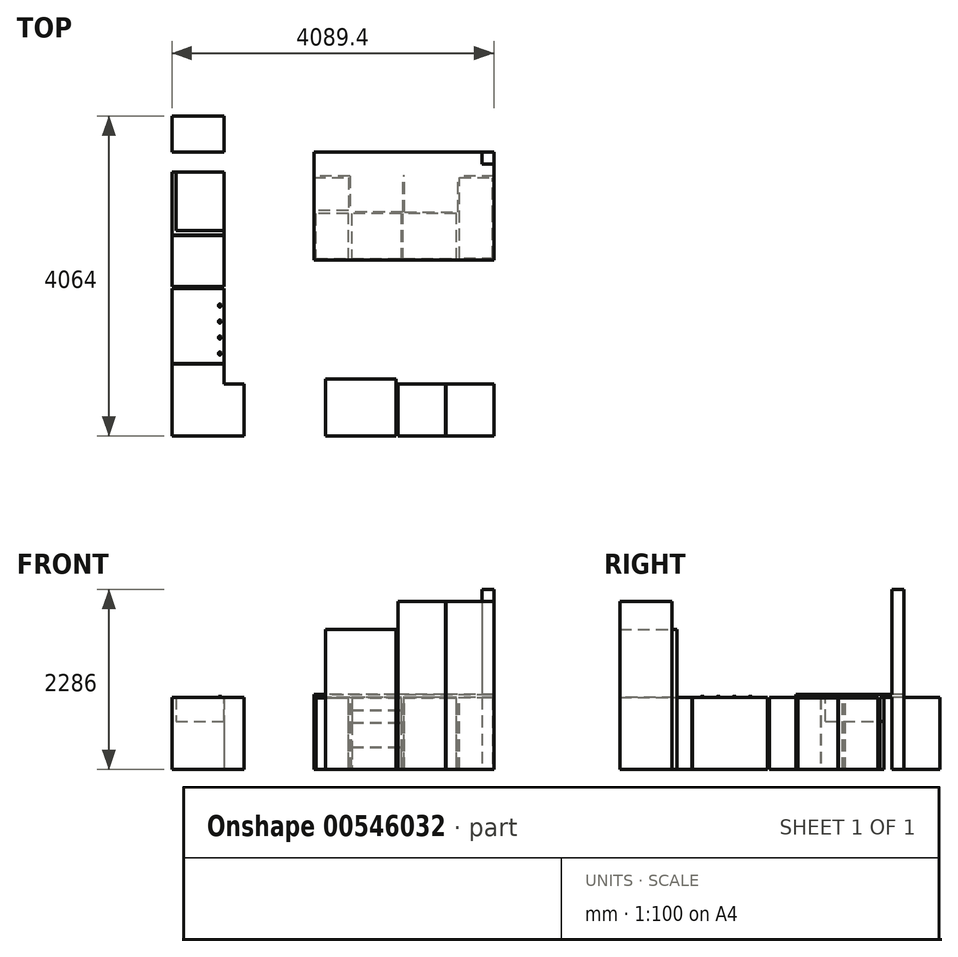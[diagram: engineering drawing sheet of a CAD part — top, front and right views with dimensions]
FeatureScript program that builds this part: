
annotation { "Feature Type Name" : "Feature", "Feature Type Description" : "" }
export const myFeature = defineFeature(function(context is Context, id is Id, definition is map)
    precondition{}
    {
        {
            var Q0;
            Q0=qCreatedBy(makeId("Top.planeOp"),FACE);
            var sketch = newSketch(context, id + "F0", { "sketchPlane" : qUnion([Q0])});
            skLineSegment(sketch, "E0.bottom", {"start": v(0, 0) * mm, "end": v(-152.4, 0) * mm});
            skLineSegment(sketch, "E0.top", {"start": v(0, -152.4) * mm, "end": v(-152.4, -152.4) * mm});
            skLineSegment(sketch, "E0.left", {"start": v(0, 0) * mm, "end": v(0, -152.4) * mm});
            skLineSegment(sketch, "E0.right", {"start": v(-152.4, 0) * mm, "end": v(-152.4, -152.4) * mm});
            skSolve(sketch);
        }
        {
            var Q0;
            Q0 = qSketchRegion(id + "F0", true);
            extrude(context, id + "F1", {"entities" : qUnion([Q0]), "depth" : 2286 * mm, "offsetDistance" : 25.4 * mm});
        }
        {
            var Q0;
            Q0=makeQuery(id+"F1.opExtrude","CAP_FACE",FACE,{"disambiguationData":[OSD([sQuery(id+"F0.wireOp",EDGE,"E0.bottom"),sQuery(id+"F0.wireOp",EDGE,"E0.top"),sQuery(id+"F0.wireOp",EDGE,"E0.left"),sQuery(id+"F0.wireOp",EDGE,"E0.right")])],"isStart":true});
            cPlane(context, id + "F2", {"entities" : qUnion([Q0]), "cplaneType" : CPlaneType.OFFSET, "offset" : 914.4 * mm, "oppositeDirection" : true, "width" : 152.4 * mm, "height" : 152.4 * mm});
        }
        {
            var Q0;
            Q0=qCreatedBy(id+"F2.planeOp",FACE);
            var sketch = newSketch(context, id + "F3", { "sketchPlane" : qUnion([Q0])});
            skLineSegment(sketch, "E1", {"start": v(0, 152.4) * mm, "end": v(0, 1371.6) * mm});
            skLineSegment(sketch, "E2", {"start": v(0, 1371.6) * mm, "end": v(-2286, 1371.6) * mm});
            skLineSegment(sketch, "E3", {"start": v(-2286, 1371.6) * mm, "end": v(-2286, 0) * mm});
            skLineSegment(sketch, "E4", {"start": v(-2286, 0) * mm, "end": v(-152.4, 0) * mm});
            skLineSegment(sketch, "E5", {"start": v(-152.4, 0) * mm, "end": v(-152.4, 152.4) * mm});
            skLineSegment(sketch, "E6", {"start": v(-152.4, 152.4) * mm, "end": v(0, 152.4) * mm});
            skSolve(sketch);
        }
        {
            var Q0;
            Q0 = qSketchRegion(id + "F3", true);
            extrude(context, id + "F4", {"entities" : qUnion([Q0]), "operationType" : NewBodyOperationType.ADD, "oppositeDirection" : true, "depth" : 38.1 * mm, "offsetDistance" : 25.4 * mm});
        }
        {
            var Q0;
            Q0=makeQuery(id+"F4.opExtrude","CAP_FACE",FACE,{"disambiguationData":[OSD([sQuery(id+"F3.wireOp",EDGE,"E1"),sQuery(id+"F3.wireOp",EDGE,"E2"),sQuery(id+"F3.wireOp",EDGE,"E3"),sQuery(id+"F3.wireOp",EDGE,"E4"),sQuery(id+"F3.wireOp",EDGE,"E5"),sQuery(id+"F3.wireOp",EDGE,"E6")])],"isStart":false});
            var sketch = newSketch(context, id + "F5", { "sketchPlane" : qUnion([Q0])});
            skLineSegment(sketch, "E7", {"start": v(-2286, -304.8) * mm, "end": v(0, -304.8) * mm});
            skSolve(sketch);
        }
        {
            var Q0;
            Q0=makeQuery(id+"F4.opExtrude","CAP_FACE",FACE,{"disambiguationData":[OSD([sQuery(id+"F3.wireOp",EDGE,"E1"),sQuery(id+"F3.wireOp",EDGE,"E2"),sQuery(id+"F3.wireOp",EDGE,"E3"),sQuery(id+"F3.wireOp",EDGE,"E4"),sQuery(id+"F3.wireOp",EDGE,"E5"),sQuery(id+"F3.wireOp",EDGE,"E6")])],"isStart":true});
            var sketch = newSketch(context, id + "F6", { "sketchPlane" : qUnion([Q0])});
            skLineSegment(sketch, "E8.bottom", {"start": v(0, 1371.6) * mm, "end": v(-457.2, 1371.6) * mm});
            skLineSegment(sketch, "E8.top", {"start": v(0, 304.8) * mm, "end": v(-457.2, 304.8) * mm});
            skLineSegment(sketch, "E8.left", {"start": v(0, 1371.6) * mm, "end": v(0, 1352.55) * mm});
            skLineSegment(sketch, "E8.right", {"start": v(-457.2, 1371.6) * mm, "end": v(-457.2, 304.8) * mm});
            skLineSegment(sketch, "E9", {"start": v(0, 1352.55) * mm, "end": v(-438.15, 1352.55) * mm});
            skLineSegment(sketch, "E10", {"start": v(-438.15, 1352.55) * mm, "end": v(-438.15, 323.85) * mm});
            skLineSegment(sketch, "E11", {"start": v(-438.15, 323.85) * mm, "end": v(0, 323.85) * mm});
            skLineSegment(sketch, "E12.trimOffspring", {"start": v(0, 323.85) * mm, "end": v(0, 304.8) * mm});
            skSolve(sketch);
        }
        {
            var Q0;
            Q0 = qSketchRegion(id + "F6", true);
            var Q1;
            Q1=makeQuery(id+"F1.opExtrude","CAP_FACE",FACE,{"disambiguationData":[OSD([sQuery(id+"F0.wireOp",EDGE,"E0.bottom"),sQuery(id+"F0.wireOp",EDGE,"E0.top"),sQuery(id+"F0.wireOp",EDGE,"E0.left"),sQuery(id+"F0.wireOp",EDGE,"E0.right")])],"isStart":true});
            extrude(context, id + "F7", {"entities" : qUnion([Q0]), "operationType" : NewBodyOperationType.ADD, "endBound" : BoundingType.UP_TO_SURFACE, "depth" : 25.4 * mm, "endBoundEntityFace" : qUnion([Q1]), "offsetDistance" : 25.4 * mm});
        }
        {
            var Q0;
            {var subQ0=sQuery(id+"F3.wireOp",EDGE,"E4");var subQ1=sQuery(id+"F3.wireOp",EDGE,"E3");var subQ2=sQuery(id+"F3.wireOp",EDGE,"E2");var subQ3=sQuery(id+"F3.wireOp",EDGE,"E1");Q0=makeQuery(id+"F7.boolean.opBoolean","SPLIT",FACE,{"disambiguationData":[TD([makeQuery(id+"F1.opExtrude","SWEPT_FACE",FACE,{"disambiguationData":[OSD([sQuery(id+"F0.wireOp",EDGE,"E0.bottom")])]})])],"derivedFrom":makeQuery(id+"F4.opExtrude","CAP_FACE",FACE,{"disambiguationData":[OSD([subQ3,subQ2,subQ1,subQ0,sQuery(id+"F3.wireOp",EDGE,"E5"),sQuery(id+"F3.wireOp",EDGE,"E6")])],"isStart":true})});}
            var sketch = newSketch(context, id + "F8", { "sketchPlane" : qUnion([Q0])});
            skLineSegment(sketch, "E13", {"start": v(-2286, 1371.6) * mm, "end": v(-2286, 762) * mm});
            skLineSegment(sketch, "E14", {"start": v(-2286, 762) * mm, "end": v(-1828.8, 762) * mm});
            skLineSegment(sketch, "E15", {"start": v(-1828.8, 762) * mm, "end": v(-1828.8, 1371.6) * mm});
            skLineSegment(sketch, "E16", {"start": v(-1828.8, 1371.6) * mm, "end": v(-1847.85, 1371.6) * mm});
            skLineSegment(sketch, "E17", {"start": v(-1847.85, 1371.6) * mm, "end": v(-1847.85, 781.05) * mm});
            skLineSegment(sketch, "E18", {"start": v(-1847.85, 781.05) * mm, "end": v(-2266.95, 781.05) * mm});
            skLineSegment(sketch, "E19", {"start": v(-2266.95, 781.05) * mm, "end": v(-2266.95, 1371.6) * mm});
            skLineSegment(sketch, "E20", {"start": v(-2266.95, 1371.6) * mm, "end": v(-2286, 1371.6) * mm});
            skSolve(sketch);
        }
        {
            var Q0;
            Q0 = qSketchRegion(id + "F8", true);
            var Q1;
            Q1=makeQuery(id+"F1.opExtrude","CAP_FACE",FACE,{"disambiguationData":[OSD([sQuery(id+"F0.wireOp",EDGE,"E0.bottom"),sQuery(id+"F0.wireOp",EDGE,"E0.top"),sQuery(id+"F0.wireOp",EDGE,"E0.left"),sQuery(id+"F0.wireOp",EDGE,"E0.right")])],"isStart":true});
            extrude(context, id + "F9", {"entities" : qUnion([Q0]), "operationType" : NewBodyOperationType.ADD, "endBound" : BoundingType.UP_TO_SURFACE, "depth" : 25.4 * mm, "endBoundEntityFace" : qUnion([Q1]), "offsetDistance" : 25.4 * mm});
        }
        {
            var Q0;
            {var subQ2=sQuery(id+"F3.wireOp",EDGE,"E4");var subQ4=sQuery(id+"F3.wireOp",EDGE,"E3");var subQ6=sQuery(id+"F3.wireOp",EDGE,"E2");var subQ8=makeQuery(id+"F1.opExtrude","SWEPT_FACE",FACE,{"disambiguationData":[OSD([sQuery(id+"F0.wireOp",EDGE,"E0.bottom")])]});var subQ9=sQuery(id+"F3.wireOp",EDGE,"E1");Q0=makeQuery(id+"F9.boolean.opBoolean","SPLIT",FACE,{"disambiguationData":[TD([subQ8])],"derivedFrom":makeQuery(id+"F7.boolean.opBoolean","SPLIT",FACE,{"disambiguationData":[TD([subQ8])],"derivedFrom":makeQuery(id+"F4.opExtrude","CAP_FACE",FACE,{"disambiguationData":[OSD([subQ9,subQ6,subQ4,subQ2,sQuery(id+"F3.wireOp",EDGE,"E5"),sQuery(id+"F3.wireOp",EDGE,"E6")])],"isStart":true})})});}
            var sketch = newSketch(context, id + "F10", { "sketchPlane" : qUnion([Q0])});
            skLineSegment(sketch, "E21", {"start": v(-2286, 762) * mm, "end": v(-1828.8, 762) * mm});
            skLineSegment(sketch, "E22", {"start": v(-1828.8, 762) * mm, "end": v(-1828.8, 304.8) * mm});
            skLineSegment(sketch, "E23", {"start": v(-1828.8, 304.8) * mm, "end": v(-2286, 304.8) * mm});
            skLineSegment(sketch, "E24", {"start": v(-2286, 304.8) * mm, "end": v(-2286, 323.85) * mm});
            skLineSegment(sketch, "E25", {"start": v(-2286, 323.85) * mm, "end": v(-1847.85, 323.85) * mm});
            skLineSegment(sketch, "E26", {"start": v(-1847.85, 323.85) * mm, "end": v(-1847.85, 742.95) * mm});
            skLineSegment(sketch, "E27", {"start": v(-1847.85, 742.95) * mm, "end": v(-2286, 742.95) * mm});
            skLineSegment(sketch, "E28", {"start": v(-2286, 742.95) * mm, "end": v(-2286, 762) * mm});
            skSolve(sketch);
        }
        {
            var Q0;
            Q0 = qSketchRegion(id + "F10", true);
            var Q1;
            Q1=makeQuery(id+"F9.opExtrude","CAP_FACE",FACE,{"disambiguationData":[OSD([sQuery(id+"F8.wireOp",EDGE,"E13"),sQuery(id+"F8.wireOp",EDGE,"E14"),sQuery(id+"F8.wireOp",EDGE,"E15"),sQuery(id+"F8.wireOp",EDGE,"E16"),sQuery(id+"F8.wireOp",EDGE,"E17"),sQuery(id+"F8.wireOp",EDGE,"E18"),sQuery(id+"F8.wireOp",EDGE,"E19"),sQuery(id+"F8.wireOp",EDGE,"E20")])],"isStart":false});
            extrude(context, id + "F11", {"entities" : qUnion([Q0]), "operationType" : NewBodyOperationType.ADD, "endBound" : BoundingType.UP_TO_SURFACE, "depth" : 25.4 * mm, "endBoundEntityFace" : qUnion([Q1]), "offsetDistance" : 25.4 * mm});
        }
        {
            var Q0;
            {var subQ2=sQuery(id+"F3.wireOp",EDGE,"E4");var subQ4=sQuery(id+"F3.wireOp",EDGE,"E3");var subQ6=sQuery(id+"F3.wireOp",EDGE,"E2");var subQ9=makeQuery(id+"F1.opExtrude","SWEPT_FACE",FACE,{"disambiguationData":[OSD([sQuery(id+"F0.wireOp",EDGE,"E0.bottom")])]});var subQ10=sQuery(id+"F3.wireOp",EDGE,"E1");Q0=makeQuery(id+"F11.boolean.opBoolean","SPLIT",FACE,{"disambiguationData":[TD([subQ9])],"derivedFrom":makeQuery(id+"F9.boolean.opBoolean","SPLIT",FACE,{"disambiguationData":[TD([subQ9])],"derivedFrom":makeQuery(id+"F7.boolean.opBoolean","SPLIT",FACE,{"disambiguationData":[TD([subQ9])],"derivedFrom":makeQuery(id+"F4.opExtrude","CAP_FACE",FACE,{"disambiguationData":[OSD([subQ10,subQ6,subQ4,subQ2,sQuery(id+"F3.wireOp",EDGE,"E5"),sQuery(id+"F3.wireOp",EDGE,"E6")])],"isStart":true})})})});}
            var sketch = newSketch(context, id + "F12", { "sketchPlane" : qUnion([Q0])});
            skLineSegment(sketch, "E29", {"start": v(-1828.8, 1371.6) * mm, "end": v(-1828.8, 762) * mm});
            skLineSegment(sketch, "E30", {"start": v(-1828.8, 762) * mm, "end": v(-457.2, 762) * mm});
            skLineSegment(sketch, "E31", {"start": v(-457.2, 762) * mm, "end": v(-457.2, 1371.6) * mm});
            skLineSegment(sketch, "E32", {"start": v(-457.2, 1371.6) * mm, "end": v(-476.25, 1371.6) * mm});
            skLineSegment(sketch, "E33", {"start": v(-476.25, 1371.6) * mm, "end": v(-476.25, 781.05) * mm});
            skLineSegment(sketch, "E34", {"start": v(-476.25, 781.05) * mm, "end": v(-1809.75, 781.05) * mm});
            skLineSegment(sketch, "E35", {"start": v(-1809.75, 781.05) * mm, "end": v(-1809.75, 1371.6) * mm});
            skLineSegment(sketch, "E36", {"start": v(-1809.75, 1371.6) * mm, "end": v(-1828.8, 1371.6) * mm});
            skSolve(sketch);
        }
        {
            var Q0;
            Q0 = qSketchRegion(id + "F12", true);
            var Q1;
            Q1=makeQuery(id+"F1.opExtrude","CAP_FACE",FACE,{"disambiguationData":[OSD([sQuery(id+"F0.wireOp",EDGE,"E0.bottom"),sQuery(id+"F0.wireOp",EDGE,"E0.top"),sQuery(id+"F0.wireOp",EDGE,"E0.left"),sQuery(id+"F0.wireOp",EDGE,"E0.right")])],"isStart":true});
            extrude(context, id + "F13", {"entities" : qUnion([Q0]), "operationType" : NewBodyOperationType.ADD, "endBound" : BoundingType.UP_TO_SURFACE, "depth" : 25.4 * mm, "endBoundEntityFace" : qUnion([Q1]), "offsetDistance" : 25.4 * mm});
        }
        {
            var Q0;
            {var subQ3=sQuery(id+"F3.wireOp",EDGE,"E2");var subQ4=makeQuery(id+"F4.opExtrude","SWEPT_FACE",FACE,{"disambiguationData":[OSD([subQ3])]});var subQ6=sQuery(id+"F3.wireOp",EDGE,"E4");var subQ8=sQuery(id+"F3.wireOp",EDGE,"E3");var subQ10=makeQuery(id+"F1.opExtrude","SWEPT_FACE",FACE,{"disambiguationData":[OSD([sQuery(id+"F0.wireOp",EDGE,"E0.bottom")])]});var subQ11=sQuery(id+"F3.wireOp",EDGE,"E1");Q0=makeQuery(id+"F13.boolean.opBoolean","SPLIT",FACE,{"disambiguationData":[TD([subQ4])],"derivedFrom":makeQuery(id+"F11.boolean.opBoolean","SPLIT",FACE,{"disambiguationData":[TD([subQ10])],"derivedFrom":makeQuery(id+"F9.boolean.opBoolean","SPLIT",FACE,{"disambiguationData":[TD([subQ10])],"derivedFrom":makeQuery(id+"F7.boolean.opBoolean","SPLIT",FACE,{"disambiguationData":[TD([subQ10])],"derivedFrom":makeQuery(id+"F4.opExtrude","CAP_FACE",FACE,{"disambiguationData":[OSD([subQ11,subQ3,subQ8,subQ6,sQuery(id+"F3.wireOp",EDGE,"E5"),sQuery(id+"F3.wireOp",EDGE,"E6")])],"isStart":true})})})})});}
            var sketch = newSketch(context, id + "F14", { "sketchPlane" : qUnion([Q0])});
            skLineSegment(sketch, "E37.bottom", {"start": v(-1174.75, 1371.6) * mm, "end": v(-1155.7, 1371.6) * mm});
            skLineSegment(sketch, "E37.top", {"start": v(-1174.75, 781.05) * mm, "end": v(-1155.7, 781.05) * mm});
            skLineSegment(sketch, "E37.left", {"start": v(-1174.75, 1371.6) * mm, "end": v(-1174.75, 781.05) * mm});
            skLineSegment(sketch, "E37.right", {"start": v(-1155.7, 1371.6) * mm, "end": v(-1155.7, 781.05) * mm});
            skSolve(sketch);
        }
        {
            var Q0;
            Q0 = qSketchRegion(id + "F14", true);
            var Q1;
            Q1=makeQuery(id+"F1.opExtrude","CAP_FACE",FACE,{"disambiguationData":[OSD([sQuery(id+"F0.wireOp",EDGE,"E0.bottom"),sQuery(id+"F0.wireOp",EDGE,"E0.top"),sQuery(id+"F0.wireOp",EDGE,"E0.left"),sQuery(id+"F0.wireOp",EDGE,"E0.right")])],"isStart":true});
            extrude(context, id + "F15", {"entities" : qUnion([Q0]), "operationType" : NewBodyOperationType.ADD, "endBound" : BoundingType.UP_TO_SURFACE, "depth" : 25.4 * mm, "endBoundEntityFace" : qUnion([Q1]), "offsetDistance" : 25.4 * mm});
        }
        {
            var Q0;
            {var subQ3=sQuery(id+"F3.wireOp",EDGE,"E4");var subQ5=sQuery(id+"F3.wireOp",EDGE,"E3");var subQ8=makeQuery(id+"F1.opExtrude","SWEPT_FACE",FACE,{"disambiguationData":[OSD([sQuery(id+"F0.wireOp",EDGE,"E0.bottom")])]});var subQ9=sQuery(id+"F3.wireOp",EDGE,"E1");var subQ21=sQuery(id+"F3.wireOp",EDGE,"E2");Q0=makeQuery(id+"F13.boolean.opBoolean","SPLIT",FACE,{"disambiguationData":[TD([subQ8])],"derivedFrom":makeQuery(id+"F11.boolean.opBoolean","SPLIT",FACE,{"disambiguationData":[TD([subQ8])],"derivedFrom":makeQuery(id+"F9.boolean.opBoolean","SPLIT",FACE,{"disambiguationData":[TD([subQ8])],"derivedFrom":makeQuery(id+"F7.boolean.opBoolean","SPLIT",FACE,{"disambiguationData":[TD([subQ8])],"derivedFrom":makeQuery(id+"F4.opExtrude","CAP_FACE",FACE,{"disambiguationData":[OSD([subQ9,subQ21,subQ5,subQ3,sQuery(id+"F3.wireOp",EDGE,"E5"),sQuery(id+"F3.wireOp",EDGE,"E6")])],"isStart":true})})})})});}
            var sketch = newSketch(context, id + "F16", { "sketchPlane" : qUnion([Q0])});
            skLineSegment(sketch, "E38.bottom", {"start": v(-1133.47, 762) * mm, "end": v(-1152.52, 762) * mm});
            skLineSegment(sketch, "E38.top", {"start": v(-1133.47, 304.8) * mm, "end": v(-1152.52, 304.8) * mm});
            skLineSegment(sketch, "E38.left", {"start": v(-1133.47, 762) * mm, "end": v(-1133.47, 304.8) * mm});
            skLineSegment(sketch, "E38.right", {"start": v(-1152.52, 762) * mm, "end": v(-1152.52, 304.8) * mm});
            skSolve(sketch);
        }
        {
            var Q0;
            Q0 = qSketchRegion(id + "F16", true);
            var Q1;
            Q1=makeQuery(id+"F15.boolean.opBoolean","MERGE",FACE,{"derivedFrom":[makeQuery(id+"F13.boolean.opBoolean","MERGE",FACE,{"derivedFrom":[makeQuery(id+"F7.opExtrude","CAP_FACE",FACE,{"disambiguationData":[OSD([sQuery(id+"F6.wireOp",EDGE,"E8.bottom"),sQuery(id+"F6.wireOp",EDGE,"E8.top"),sQuery(id+"F6.wireOp",EDGE,"E8.left"),sQuery(id+"F6.wireOp",EDGE,"E8.right"),sQuery(id+"F6.wireOp",EDGE,"E9"),sQuery(id+"F6.wireOp",EDGE,"E10"),sQuery(id+"F6.wireOp",EDGE,"E11"),sQuery(id+"F6.wireOp",EDGE,"E12.trimOffspring")])],"isStart":false}),makeQuery(id+"F11.boolean.opBoolean","MERGE",FACE,{"derivedFrom":[makeQuery(id+"F9.opExtrude","CAP_FACE",FACE,{"disambiguationData":[OSD([sQuery(id+"F8.wireOp",EDGE,"E13"),sQuery(id+"F8.wireOp",EDGE,"E14"),sQuery(id+"F8.wireOp",EDGE,"E15"),sQuery(id+"F8.wireOp",EDGE,"E16"),sQuery(id+"F8.wireOp",EDGE,"E17"),sQuery(id+"F8.wireOp",EDGE,"E18"),sQuery(id+"F8.wireOp",EDGE,"E19"),sQuery(id+"F8.wireOp",EDGE,"E20")])],"isStart":false}),makeQuery(id+"F11.opExtrude","CAP_FACE",FACE,{"disambiguationData":[OSD([sQuery(id+"F10.wireOp",EDGE,"E21"),sQuery(id+"F10.wireOp",EDGE,"E22"),sQuery(id+"F10.wireOp",EDGE,"E23"),sQuery(id+"F10.wireOp",EDGE,"E24"),sQuery(id+"F10.wireOp",EDGE,"E25"),sQuery(id+"F10.wireOp",EDGE,"E26"),sQuery(id+"F10.wireOp",EDGE,"E27"),sQuery(id+"F10.wireOp",EDGE,"E28")])],"isStart":false})]}),makeQuery(id+"F13.opExtrude","CAP_FACE",FACE,{"disambiguationData":[OSD([sQuery(id+"F12.wireOp",EDGE,"E29"),sQuery(id+"F12.wireOp",EDGE,"E30"),sQuery(id+"F12.wireOp",EDGE,"E31"),sQuery(id+"F12.wireOp",EDGE,"E32"),sQuery(id+"F12.wireOp",EDGE,"E33"),sQuery(id+"F12.wireOp",EDGE,"E34"),sQuery(id+"F12.wireOp",EDGE,"E35"),sQuery(id+"F12.wireOp",EDGE,"E36")])],"isStart":false})]}),makeQuery(id+"F15.opExtrude","CAP_FACE",FACE,{"disambiguationData":[OSD([sQuery(id+"F14.wireOp",EDGE,"E37.bottom"),sQuery(id+"F14.wireOp",EDGE,"E37.top"),sQuery(id+"F14.wireOp",EDGE,"E37.left"),sQuery(id+"F14.wireOp",EDGE,"E37.right")])],"isStart":false})]});
            extrude(context, id + "F17", {"entities" : qUnion([Q0]), "operationType" : NewBodyOperationType.ADD, "endBound" : BoundingType.UP_TO_SURFACE, "depth" : 25.4 * mm, "endBoundEntityFace" : qUnion([Q1]), "offsetDistance" : 25.4 * mm});
        }
        {
            var Q0;
            Q0=makeQuery(id+"F7.boolean.opBoolean","MERGE",FACE,{"derivedFrom":[makeQuery(id+"F4.boolean.opBoolean","MERGE",FACE,{"derivedFrom":[makeQuery(id+"F1.opExtrude","SWEPT_FACE",FACE,{"disambiguationData":[OSD([sQuery(id+"F0.wireOp",EDGE,"E0.left")])]}),makeQuery(id+"F4.opExtrude","SWEPT_FACE",FACE,{"disambiguationData":[OSD([sQuery(id+"F3.wireOp",EDGE,"E1")])]})]}),makeQuery(id+"F7.opExtrude","SWEPT_FACE",FACE,{"disambiguationData":[OSD([sQuery(id+"F6.wireOp",EDGE,"E8.left")])]}),makeQuery(id+"F7.opExtrude","SWEPT_FACE",FACE,{"disambiguationData":[OSD([sQuery(id+"F6.wireOp",EDGE,"E12.trimOffspring")])]})]});
            var sketch = newSketch(context, id + "F18", { "sketchPlane" : qUnion([Q0])});
            skPoint(sketch, "E39.oppositeSnap0", {"position": v(-838.2, 914.4) * mm});
            skLineSegment(sketch, "E39.bottom", {"start": v(-1346.2, 908.05) * mm, "end": v(-838.2, 908.05) * mm});
            skLineSegment(sketch, "E39.top", {"start": v(-1346.2, 0) * mm, "end": v(-838.2, 0) * mm});
            skLineSegment(sketch, "E39.left", {"start": v(-1346.2, 908.05) * mm, "end": v(-1346.2, 0) * mm});
            skLineSegment(sketch, "E39.right", {"start": v(-838.2, 908.05) * mm, "end": v(-838.2, 0) * mm});
            skSolve(sketch);
        }
        {
            var Q0;
            Q0 = qSketchRegion(id + "F18", true);
            extrude(context, id + "F19", {"entities" : qUnion([Q0]), "oppositeDirection" : true, "depth" : 19.05 * mm, "offsetDistance" : 25.4 * mm});
        }
        {
            var Q0;
            Q0=makeQuery(id+"F7.boolean.opBoolean","MERGE",FACE,{"derivedFrom":[makeQuery(id+"F4.boolean.opBoolean","MERGE",FACE,{"derivedFrom":[makeQuery(id+"F1.opExtrude","SWEPT_FACE",FACE,{"disambiguationData":[OSD([sQuery(id+"F0.wireOp",EDGE,"E0.left")])]}),makeQuery(id+"F4.opExtrude","SWEPT_FACE",FACE,{"disambiguationData":[OSD([sQuery(id+"F3.wireOp",EDGE,"E1")])]})]}),makeQuery(id+"F7.opExtrude","SWEPT_FACE",FACE,{"disambiguationData":[OSD([sQuery(id+"F6.wireOp",EDGE,"E8.left")])]}),makeQuery(id+"F7.opExtrude","SWEPT_FACE",FACE,{"disambiguationData":[OSD([sQuery(id+"F6.wireOp",EDGE,"E12.trimOffspring")])]})]});
            var sketch = newSketch(context, id + "F20", { "sketchPlane" : qUnion([Q0])});
            skPoint(sketch, "E40.firstSnap0", {"position": v(-831.85, 914.4) * mm});
            skLineSegment(sketch, "E40.bottom", {"start": v(-831.85, 908.05) * mm, "end": v(-330.2, 908.05) * mm});
            skLineSegment(sketch, "E40.top", {"start": v(-831.85, 0) * mm, "end": v(-330.2, 0) * mm});
            skLineSegment(sketch, "E40.left", {"start": v(-831.85, 908.05) * mm, "end": v(-831.85, 0) * mm});
            skLineSegment(sketch, "E40.right", {"start": v(-330.2, 908.05) * mm, "end": v(-330.2, 0) * mm});
            skSolve(sketch);
        }
        {
            var Q0;
            Q0 = qSketchRegion(id + "F20", true);
            extrude(context, id + "F21", {"entities" : qUnion([Q0]), "operationType" : NewBodyOperationType.ADD, "oppositeDirection" : true, "depth" : 19.05 * mm, "offsetDistance" : 25.4 * mm});
        }
        {
            var Q0;
            Q0=makeQuery(id+"F15.boolean.opBoolean","MERGE",FACE,{"derivedFrom":[makeQuery(id+"F13.boolean.opBoolean","MERGE",FACE,{"derivedFrom":[makeQuery(id+"F9.boolean.opBoolean","MERGE",FACE,{"derivedFrom":[makeQuery(id+"F7.boolean.opBoolean","MERGE",FACE,{"derivedFrom":[makeQuery(id+"F4.opExtrude","SWEPT_FACE",FACE,{"disambiguationData":[OSD([sQuery(id+"F3.wireOp",EDGE,"E2")])]}),makeQuery(id+"F7.opExtrude","SWEPT_FACE",FACE,{"disambiguationData":[OSD([sQuery(id+"F6.wireOp",EDGE,"E8.bottom")])]})]}),makeQuery(id+"F9.opExtrude","SWEPT_FACE",FACE,{"disambiguationData":[OSD([sQuery(id+"F8.wireOp",EDGE,"E16")])]}),makeQuery(id+"F9.opExtrude","SWEPT_FACE",FACE,{"disambiguationData":[OSD([sQuery(id+"F8.wireOp",EDGE,"E20")])]})]}),makeQuery(id+"F13.opExtrude","SWEPT_FACE",FACE,{"disambiguationData":[OSD([sQuery(id+"F12.wireOp",EDGE,"E32")])]}),makeQuery(id+"F13.opExtrude","SWEPT_FACE",FACE,{"disambiguationData":[OSD([sQuery(id+"F12.wireOp",EDGE,"E36")])]})]}),makeQuery(id+"F15.opExtrude","SWEPT_FACE",FACE,{"disambiguationData":[OSD([sQuery(id+"F14.wireOp",EDGE,"E37.bottom")])]})]});
            var sketch = newSketch(context, id + "F22", { "sketchPlane" : qUnion([Q0])});
            skLineSegment(sketch, "E41.bottom", {"start": v(-1803.4, 908.05) * mm, "end": v(-1181.1, 908.05) * mm});
            skLineSegment(sketch, "E41.top", {"start": v(-1803.4, 755.65) * mm, "end": v(-1181.1, 755.65) * mm});
            skLineSegment(sketch, "E41.left", {"start": v(-1803.4, 908.05) * mm, "end": v(-1803.4, 755.65) * mm});
            skLineSegment(sketch, "E41.right", {"start": v(-1181.1, 908.05) * mm, "end": v(-1181.1, 755.65) * mm});
            skLineSegment(sketch, "E42.bottom", {"start": v(-1803.4, 749.3) * mm, "end": v(-1181.1, 749.3) * mm});
            skLineSegment(sketch, "E42.top", {"start": v(-1803.4, 596.9) * mm, "end": v(-1181.1, 596.9) * mm});
            skLineSegment(sketch, "E42.left", {"start": v(-1803.4, 749.3) * mm, "end": v(-1803.4, 596.9) * mm});
            skLineSegment(sketch, "E42.right", {"start": v(-1181.1, 749.3) * mm, "end": v(-1181.1, 596.9) * mm});
            skLineSegment(sketch, "E43.bottom", {"start": v(-1803.4, 590.55) * mm, "end": v(-1181.1, 590.55) * mm});
            skLineSegment(sketch, "E43.top", {"start": v(-1803.4, 285.75) * mm, "end": v(-1181.1, 285.75) * mm});
            skLineSegment(sketch, "E43.left", {"start": v(-1803.4, 590.55) * mm, "end": v(-1803.4, 285.75) * mm});
            skLineSegment(sketch, "E43.right", {"start": v(-1181.1, 590.55) * mm, "end": v(-1181.1, 285.75) * mm});
            skLineSegment(sketch, "E44.bottom", {"start": v(-1803.4, 279.4) * mm, "end": v(-1181.1, 279.4) * mm});
            skLineSegment(sketch, "E44.top", {"start": v(-1803.4, 0) * mm, "end": v(-1181.1, 0) * mm});
            skLineSegment(sketch, "E44.left", {"start": v(-1803.4, 279.4) * mm, "end": v(-1803.4, 0) * mm});
            skLineSegment(sketch, "E44.right", {"start": v(-1181.1, 279.4) * mm, "end": v(-1181.1, 0) * mm});
            skSolve(sketch);
        }
        {
            var Q0;
            Q0 = qSketchRegion(id + "F22", true);
            extrude(context, id + "F23", {"entities" : qUnion([Q0]), "oppositeDirection" : true, "depth" : 19.05 * mm, "offsetDistance" : 25.4 * mm});
        }
        {
            var Q0;
            Q0=makeQuery(id+"F15.boolean.opBoolean","MERGE",FACE,{"derivedFrom":[makeQuery(id+"F13.boolean.opBoolean","MERGE",FACE,{"derivedFrom":[makeQuery(id+"F9.boolean.opBoolean","MERGE",FACE,{"derivedFrom":[makeQuery(id+"F7.boolean.opBoolean","MERGE",FACE,{"derivedFrom":[makeQuery(id+"F4.opExtrude","SWEPT_FACE",FACE,{"disambiguationData":[OSD([sQuery(id+"F3.wireOp",EDGE,"E2")])]}),makeQuery(id+"F7.opExtrude","SWEPT_FACE",FACE,{"disambiguationData":[OSD([sQuery(id+"F6.wireOp",EDGE,"E8.bottom")])]})]}),makeQuery(id+"F9.opExtrude","SWEPT_FACE",FACE,{"disambiguationData":[OSD([sQuery(id+"F8.wireOp",EDGE,"E16")])]}),makeQuery(id+"F9.opExtrude","SWEPT_FACE",FACE,{"disambiguationData":[OSD([sQuery(id+"F8.wireOp",EDGE,"E20")])]})]}),makeQuery(id+"F13.opExtrude","SWEPT_FACE",FACE,{"disambiguationData":[OSD([sQuery(id+"F12.wireOp",EDGE,"E32")])]}),makeQuery(id+"F13.opExtrude","SWEPT_FACE",FACE,{"disambiguationData":[OSD([sQuery(id+"F12.wireOp",EDGE,"E36")])]})]}),makeQuery(id+"F15.opExtrude","SWEPT_FACE",FACE,{"disambiguationData":[OSD([sQuery(id+"F14.wireOp",EDGE,"E37.bottom")])]})]});
            var sketch = newSketch(context, id + "F24", { "sketchPlane" : qUnion([Q0])});
            skLineSegment(sketch, "E45.bottom", {"start": v(-2260.6, 908.05) * mm, "end": v(-1854.2, 908.05) * mm});
            skLineSegment(sketch, "E45.top", {"start": v(-2260.6, 0) * mm, "end": v(-1854.2, 0) * mm});
            skLineSegment(sketch, "E45.left", {"start": v(-2260.6, 908.05) * mm, "end": v(-2260.6, 0) * mm});
            skLineSegment(sketch, "E45.right", {"start": v(-1854.2, 908.05) * mm, "end": v(-1854.2, 0) * mm});
            skSolve(sketch);
        }
        {
            var Q0;
            Q0 = qSketchRegion(id + "F24", true);
            extrude(context, id + "F25", {"entities" : qUnion([Q0]), "oppositeDirection" : true, "depth" : 19.05 * mm, "offsetDistance" : 25.4 * mm});
        }
        {
            var Q0;
            Q0=makeQuery(id+"F15.boolean.opBoolean","MERGE",FACE,{"derivedFrom":[makeQuery(id+"F13.boolean.opBoolean","MERGE",FACE,{"derivedFrom":[makeQuery(id+"F9.boolean.opBoolean","MERGE",FACE,{"derivedFrom":[makeQuery(id+"F7.boolean.opBoolean","MERGE",FACE,{"derivedFrom":[makeQuery(id+"F4.opExtrude","SWEPT_FACE",FACE,{"disambiguationData":[OSD([sQuery(id+"F3.wireOp",EDGE,"E2")])]}),makeQuery(id+"F7.opExtrude","SWEPT_FACE",FACE,{"disambiguationData":[OSD([sQuery(id+"F6.wireOp",EDGE,"E8.bottom")])]})]}),makeQuery(id+"F9.opExtrude","SWEPT_FACE",FACE,{"disambiguationData":[OSD([sQuery(id+"F8.wireOp",EDGE,"E16")])]}),makeQuery(id+"F9.opExtrude","SWEPT_FACE",FACE,{"disambiguationData":[OSD([sQuery(id+"F8.wireOp",EDGE,"E20")])]})]}),makeQuery(id+"F13.opExtrude","SWEPT_FACE",FACE,{"disambiguationData":[OSD([sQuery(id+"F12.wireOp",EDGE,"E32")])]}),makeQuery(id+"F13.opExtrude","SWEPT_FACE",FACE,{"disambiguationData":[OSD([sQuery(id+"F12.wireOp",EDGE,"E36")])]})]}),makeQuery(id+"F15.opExtrude","SWEPT_FACE",FACE,{"disambiguationData":[OSD([sQuery(id+"F14.wireOp",EDGE,"E37.bottom")])]})]});
            var sketch = newSketch(context, id + "F26", { "sketchPlane" : qUnion([Q0])});
            skLineSegment(sketch, "E46.bottom", {"start": v(-1149.35, 908.05) * mm, "end": v(-482.6, 908.05) * mm});
            skLineSegment(sketch, "E46.top", {"start": v(-1149.35, 0) * mm, "end": v(-482.6, 0) * mm});
            skLineSegment(sketch, "E46.left", {"start": v(-1149.35, 908.05) * mm, "end": v(-1149.35, 0) * mm});
            skLineSegment(sketch, "E46.right", {"start": v(-482.6, 908.05) * mm, "end": v(-482.6, 0) * mm});
            skSolve(sketch);
        }
        {
            var Q0;
            Q0 = qSketchRegion(id + "F26", true);
            extrude(context, id + "F27", {"entities" : qUnion([Q0]), "oppositeDirection" : true, "depth" : 19.05 * mm, "offsetDistance" : 25.4 * mm});
        }
        {
            var Q0;
            Q0=makeQuery(id+"F1.opExtrude","CAP_FACE",FACE,{"disambiguationData":[OSD([sQuery(id+"F0.wireOp",EDGE,"E0.bottom"),sQuery(id+"F0.wireOp",EDGE,"E0.top"),sQuery(id+"F0.wireOp",EDGE,"E0.left"),sQuery(id+"F0.wireOp",EDGE,"E0.right")])],"isStart":true});
            var sketch = newSketch(context, id + "F28", { "sketchPlane" : qUnion([Q0])});
            skLineSegment(sketch, "E47.bottom", {"start": v(0, 0) * mm, "end": v(-4089.4, 0) * mm});
            skLineSegment(sketch, "E47.top", {"start": v(0, 3606.8) * mm, "end": v(-4089.4, 3606.8) * mm});
            skLineSegment(sketch, "E47.left", {"start": v(0, 0) * mm, "end": v(0, 3606.8) * mm});
            skLineSegment(sketch, "E47.right", {"start": v(-4089.4, 0) * mm, "end": v(-4089.4, 3606.8) * mm});
            skSolve(sketch);
        }
        {
            var Q0;
            {var subQ4=makeQuery(id+"F1.opExtrude","CAP_EDGE",EDGE,{"disambiguationData":[OSD([sQuery(id+"F0.wireOp",EDGE,"E0.top")])],"isStart":true});Q0=makeQuery(id+"F28.imprint","IMPRINT",FACE,{"disambiguationData":[TD([[makeQuery(id+"F28.imprint","IMPRINT",EDGE,{"derivedFrom":subQ4}),1.0]])]});}
            var sketch = newSketch(context, id + "F29", { "sketchPlane" : qUnion([Q0])});
            skLineSegment(sketch, "E48.bottom", {"start": v(0, 3606.8) * mm, "end": v(-609.6, 3606.8) * mm});
            skLineSegment(sketch, "E48.top", {"start": v(0, 2946.4) * mm, "end": v(-609.6, 2946.4) * mm});
            skLineSegment(sketch, "E48.left", {"start": v(0, 3606.8) * mm, "end": v(0, 2946.4) * mm});
            skLineSegment(sketch, "E48.right", {"start": v(-609.6, 3606.8) * mm, "end": v(-609.6, 2946.4) * mm});
            skSolve(sketch);
        }
        {
            var Q0;
            Q0 = qSketchRegion(id + "F29", true);
            extrude(context, id + "F30", {"entities" : qUnion([Q0]), "oppositeDirection" : true, "depth" : 2133.6 * mm, "offsetDistance" : 25.4 * mm});
        }
        {
            var Q0;
            {var subQ4=makeQuery(id+"F1.opExtrude","CAP_EDGE",EDGE,{"disambiguationData":[OSD([sQuery(id+"F0.wireOp",EDGE,"E0.top")])],"isStart":true});Q0=makeQuery(id+"F28.imprint","IMPRINT",FACE,{"disambiguationData":[TD([[makeQuery(id+"F28.imprint","IMPRINT",EDGE,{"derivedFrom":subQ4}),1.0]])]});}
            var sketch = newSketch(context, id + "F31", { "sketchPlane" : qUnion([Q0])});
            skLineSegment(sketch, "E49.bottom", {"start": v(-615.95, 3606.8) * mm, "end": v(-1219.2, 3606.8) * mm});
            skLineSegment(sketch, "E49.top", {"start": v(-615.95, 2946.4) * mm, "end": v(-1219.2, 2946.4) * mm});
            skLineSegment(sketch, "E49.left", {"start": v(-1219.2, 3606.8) * mm, "end": v(-1219.2, 2946.4) * mm});
            skLineSegment(sketch, "E49.right", {"start": v(-615.95, 3606.8) * mm, "end": v(-615.95, 2946.4) * mm});
            skSolve(sketch);
        }
        {
            var Q0;
            Q0 = qSketchRegion(id + "F31", true);
            var Q1;
            Q1=makeQuery(id+"F30.opExtrude","CAP_FACE",FACE,{"disambiguationData":[OSD([sQuery(id+"F29.wireOp",EDGE,"E48.bottom"),sQuery(id+"F29.wireOp",EDGE,"E48.top"),sQuery(id+"F29.wireOp",EDGE,"E48.left"),sQuery(id+"F29.wireOp",EDGE,"E48.right")])],"isStart":false});
            extrude(context, id + "F32", {"entities" : qUnion([Q0]), "endBound" : BoundingType.UP_TO_SURFACE, "oppositeDirection" : true, "depth" : 25.4 * mm, "endBoundEntityFace" : qUnion([Q1]), "offsetDistance" : 25.4 * mm});
        }
        {
            var Q0;
            {var subQ4=makeQuery(id+"F1.opExtrude","CAP_EDGE",EDGE,{"disambiguationData":[OSD([sQuery(id+"F0.wireOp",EDGE,"E0.top")])],"isStart":true});Q0=makeQuery(id+"F28.imprint","IMPRINT",FACE,{"disambiguationData":[TD([[makeQuery(id+"F28.imprint","IMPRINT",EDGE,{"derivedFrom":subQ4}),1.0]])]});}
            var sketch = newSketch(context, id + "F33", { "sketchPlane" : qUnion([Q0])});
            skLineSegment(sketch, "E50.bottom", {"start": v(-1244.6, 3606.8) * mm, "end": v(-2139.95, 3606.8) * mm});
            skLineSegment(sketch, "E50.top", {"start": v(-1244.6, 2882.9) * mm, "end": v(-2139.95, 2882.9) * mm});
            skLineSegment(sketch, "E50.left", {"start": v(-1244.6, 3606.8) * mm, "end": v(-1244.6, 2882.9) * mm});
            skLineSegment(sketch, "E50.right", {"start": v(-2139.95, 3606.8) * mm, "end": v(-2139.95, 2882.9) * mm});
            skSolve(sketch);
        }
        {
            var Q0;
            Q0 = qSketchRegion(id + "F33", true);
            extrude(context, id + "F34", {"entities" : qUnion([Q0]), "oppositeDirection" : true, "depth" : 1778 * mm, "offsetDistance" : 25.4 * mm});
        }
        {
            var Q0;
            Q0=qCreatedBy(makeId("Right.planeOp"),FACE);
            var Q1;
            Q1=sQuery(id+"F28.wireOp",VERTEX,"E47.right.start");
            cPlane(context, id + "F35", {"entities" : qUnion([Q0, Q1]), "cplaneType" : CPlaneType.PLANE_POINT, "offset" : 25.4 * mm, "width" : 152.4 * mm, "height" : 152.4 * mm});
        }
        {
            var Q0;
            Q0=qCreatedBy(id+"F35.planeOp",FACE);
            var sketch = newSketch(context, id + "F36", { "sketchPlane" : qUnion([Q0])});
            skLineSegment(sketch, "E51.bottom", {"start": v(0, 2057.4) * mm, "end": v(-1447.8, 2057.4) * mm});
            skLineSegment(sketch, "E51.top", {"start": v(0, 1193.8) * mm, "end": v(-1447.8, 1193.8) * mm});
            skLineSegment(sketch, "E51.left", {"start": v(0, 2057.4) * mm, "end": v(0, 1193.8) * mm});
            skLineSegment(sketch, "E51.right", {"start": v(-1447.8, 2057.4) * mm, "end": v(-1447.8, 1193.8) * mm});
            skSolve(sketch);
        }
        {
            var Q0;
            {var subQ2=sQuery(id+"F28.wireOp",EDGE,"E47.top");Q0=makeQuery(id+"F28.imprint","IMPRINT",FACE,{"disambiguationData":[TD([[makeQuery(id+"F28.imprint","IMPRINT",EDGE,{"derivedFrom":subQ2}),1.0]])]});}
            var sketch = newSketch(context, id + "F37", { "sketchPlane" : qUnion([Q0])});
            skLineSegment(sketch, "E52.bottom", {"start": v(-4089.4, 1054.1) * mm, "end": v(-3429, 1054.1) * mm});
            skLineSegment(sketch, "E52.top", {"start": v(-4089.4, 254) * mm, "end": v(-3429, 254) * mm});
            skLineSegment(sketch, "E52.left", {"start": v(-4089.4, 1054.1) * mm, "end": v(-4089.4, 254) * mm});
            skLineSegment(sketch, "E52.right", {"start": v(-3429, 1054.1) * mm, "end": v(-3429, 254) * mm});
            skSolve(sketch);
        }
        {
            var Q0;
            Q0 = qSketchRegion(id + "F37", true);
            extrude(context, id + "F38", {"entities" : qUnion([Q0]), "oppositeDirection" : true, "depth" : 914.4 * mm, "offsetDistance" : 25.4 * mm});
        }
        {
            var Q0;
            {var subQ4=makeQuery(id+"F1.opExtrude","CAP_EDGE",EDGE,{"disambiguationData":[OSD([sQuery(id+"F0.wireOp",EDGE,"E0.top")])],"isStart":true});Q0=makeQuery(id+"F28.imprint","IMPRINT",FACE,{"disambiguationData":[TD([[makeQuery(id+"F28.imprint","IMPRINT",EDGE,{"derivedFrom":subQ4}),1.0]])]});}
            var sketch = newSketch(context, id + "F39", { "sketchPlane" : qUnion([Q0])});
            skLineSegment(sketch, "E53", {"start": v(-3175, 3606.8) * mm, "end": v(-3175, 2946.4) * mm});
            skLineSegment(sketch, "E54", {"start": v(-3175, 2946.4) * mm, "end": v(-3429, 2946.4) * mm});
            skLineSegment(sketch, "E55", {"start": v(-3429, 2946.4) * mm, "end": v(-3429, 2692.4) * mm});
            skLineSegment(sketch, "E56", {"start": v(-3429, 2692.4) * mm, "end": v(-4089.4, 2692.4) * mm});
            skLineSegment(sketch, "E57", {"start": v(-4089.4, 2692.4) * mm, "end": v(-4089.4, 3606.8) * mm});
            skLineSegment(sketch, "E58", {"start": v(-4089.4, 3606.8) * mm, "end": v(-3175, 3606.8) * mm});
            skSolve(sketch);
        }
        {
            var Q0;
            Q0 = qSketchRegion(id + "F39", true);
            extrude(context, id + "F40", {"entities" : qUnion([Q0]), "oppositeDirection" : true, "depth" : 914.4 * mm, "offsetDistance" : 25.4 * mm});
        }
        {
            var Q0;
            {var subQ4=makeQuery(id+"F1.opExtrude","CAP_EDGE",EDGE,{"disambiguationData":[OSD([sQuery(id+"F0.wireOp",EDGE,"E0.top")])],"isStart":true});Q0=makeQuery(id+"F28.imprint","IMPRINT",FACE,{"disambiguationData":[TD([[makeQuery(id+"F28.imprint","IMPRINT",EDGE,{"derivedFrom":subQ4}),1.0]])]});}
            var sketch = newSketch(context, id + "F41", { "sketchPlane" : qUnion([Q0])});
            skLineSegment(sketch, "E59.bottom", {"start": v(-4089.4, 2686.05) * mm, "end": v(-3429, 2686.05) * mm});
            skLineSegment(sketch, "E59.top", {"start": v(-4089.4, 1733.55) * mm, "end": v(-3429, 1733.55) * mm});
            skLineSegment(sketch, "E59.left", {"start": v(-4089.4, 2686.05) * mm, "end": v(-4089.4, 1733.55) * mm});
            skLineSegment(sketch, "E59.right", {"start": v(-3429, 2686.05) * mm, "end": v(-3429, 1733.55) * mm});
            skSolve(sketch);
        }
        {
            var Q0;
            Q0 = qSketchRegion(id + "F41", true);
            extrude(context, id + "F42", {"entities" : qUnion([Q0]), "oppositeDirection" : true, "depth" : 914.4 * mm, "offsetDistance" : 25.4 * mm});
        }
        {
            var Q0;
            {var subQ4=makeQuery(id+"F1.opExtrude","CAP_EDGE",EDGE,{"disambiguationData":[OSD([sQuery(id+"F0.wireOp",EDGE,"E0.top")])],"isStart":true});Q0=makeQuery(id+"F28.imprint","IMPRINT",FACE,{"disambiguationData":[TD([[makeQuery(id+"F28.imprint","IMPRINT",EDGE,{"derivedFrom":subQ4}),1.0]])]});}
            var sketch = newSketch(context, id + "F43", { "sketchPlane" : qUnion([Q0])});
            skLineSegment(sketch, "E60.bottom", {"start": v(-4089.4, 0) * mm, "end": v(-3429, 0) * mm});
            skLineSegment(sketch, "E60.top", {"start": v(-4089.4, -457.2) * mm, "end": v(-3429, -457.2) * mm});
            skLineSegment(sketch, "E60.left", {"start": v(-4089.4, 0) * mm, "end": v(-4089.4, -457.2) * mm});
            skLineSegment(sketch, "E60.right", {"start": v(-3429, 0) * mm, "end": v(-3429, -457.2) * mm});
            skSolve(sketch);
        }
        {
            var Q0;
            Q0 = qSketchRegion(id + "F43", true);
            extrude(context, id + "F44", {"entities" : qUnion([Q0]), "oppositeDirection" : true, "depth" : 914.4 * mm, "offsetDistance" : 25.4 * mm});
        }
        {
            var Q0;
            Q0=makeQuery(id+"F42.opExtrude","CAP_FACE",FACE,{"disambiguationData":[OSD([sQuery(id+"F41.wireOp",EDGE,"E59.bottom"),sQuery(id+"F41.wireOp",EDGE,"E59.top"),sQuery(id+"F41.wireOp",EDGE,"E59.left"),sQuery(id+"F41.wireOp",EDGE,"E59.right")])],"isStart":false});
            var sketch = newSketch(context, id + "F45", { "sketchPlane" : qUnion([Q0])});
            skLineSegment(sketch, "E61", {"start": v(-3479.8, -2686.05) * mm, "end": v(-3479.8, -1733.55) * mm});
            skCircle(sketch, "E62", {"center": v(-3479.8, -2559.05) * mm, "radius": 19.05 * mm});
            skCircle(sketch, "E63.0.1.0", {"center": v(-3479.8, -2355.85) * mm, "radius": 19.05 * mm});
            skCircle(sketch, "E63.0.2.0", {"center": v(-3479.8, -2152.65) * mm, "radius": 19.05 * mm});
            skCircle(sketch, "E63.0.3.0", {"center": v(-3479.8, -1949.45) * mm, "radius": 19.05 * mm});
            skLineSegment(sketch, "E63.direction1", {"start": v(-3479.8, -2559.05) * mm, "end": v(-3454.4, -2559.05) * mm, "construction": true});
            skLineSegment(sketch, "E63.direction2", {"start": v(-3479.8, -2559.05) * mm, "end": v(-3479.8, -2355.85) * mm, "construction": true});
            skSolve(sketch);
        }
        {
            var Q0;
            {var subQ4=makeQuery(id+"F1.opExtrude","CAP_EDGE",EDGE,{"disambiguationData":[OSD([sQuery(id+"F0.wireOp",EDGE,"E0.top")])],"isStart":true});Q0=makeQuery(id+"F28.imprint","IMPRINT",FACE,{"disambiguationData":[TD([[makeQuery(id+"F28.imprint","IMPRINT",EDGE,{"derivedFrom":subQ4}),1.0]])]});}
            var sketch = newSketch(context, id + "F46", { "sketchPlane" : qUnion([Q0])});
            skLineSegment(sketch, "E64.bottom", {"start": v(-4089.4, 1708.15) * mm, "end": v(-3429, 1708.15) * mm});
            skLineSegment(sketch, "E64.top", {"start": v(-4089.4, 1060.45) * mm, "end": v(-3429, 1060.45) * mm});
            skLineSegment(sketch, "E64.left", {"start": v(-4089.4, 1708.15) * mm, "end": v(-4089.4, 1060.45) * mm});
            skLineSegment(sketch, "E64.right", {"start": v(-3429, 1708.15) * mm, "end": v(-3429, 1060.45) * mm});
            skSolve(sketch);
        }
        {
            var Q0;
            Q0 = qSketchRegion(id + "F46", true);
            extrude(context, id + "F47", {"entities" : qUnion([Q0]), "oppositeDirection" : true, "depth" : 914.4 * mm, "offsetDistance" : 25.4 * mm});
        }
        {
            var Q0;
            Q0 = qSketchRegion(id + "F45", true);
            extrude(context, id + "F48", {"entities" : qUnion([Q0]), "operationType" : NewBodyOperationType.ADD, "depth" : 12.7 * mm, "offsetDistance" : 25.4 * mm});
        }
        {
            var Q0;
            Q0=makeQuery(id+"F38.opExtrude","CAP_FACE",FACE,{"disambiguationData":[OSD([sQuery(id+"F37.wireOp",EDGE,"E52.bottom"),sQuery(id+"F37.wireOp",EDGE,"E52.top"),sQuery(id+"F37.wireOp",EDGE,"E52.left"),sQuery(id+"F37.wireOp",EDGE,"E52.right")])],"isStart":false});
            var sketch = newSketch(context, id + "F49", { "sketchPlane" : qUnion([Q0])});
            skLineSegment(sketch, "E65.bottom", {"start": v(-4038.6, -996.95) * mm, "end": v(-3429, -996.95) * mm});
            skLineSegment(sketch, "E65.top", {"start": v(-4038.6, -234.95) * mm, "end": v(-3429, -234.95) * mm});
            skLineSegment(sketch, "E65.left", {"start": v(-4038.6, -996.95) * mm, "end": v(-4038.6, -234.95) * mm});
            skLineSegment(sketch, "E65.right", {"start": v(-3429, -996.95) * mm, "end": v(-3429, -234.95) * mm});
            skSolve(sketch);
        }
        {
            var Q0;
            Q0 = qSketchRegion(id + "F49", true);
            extrude(context, id + "F50", {"entities" : qUnion([Q0]), "operationType" : NewBodyOperationType.REMOVE, "oppositeDirection" : true, "depth" : 304.8 * mm, "offsetDistance" : 25.4 * mm});
        }
    });
